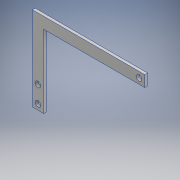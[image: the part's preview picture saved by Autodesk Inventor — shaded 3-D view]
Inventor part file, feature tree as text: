
AUTODESK INVENTOR PART (.ipt)
format: ipt  version: 2018.1 (Build 221171000, 171)  size: 113,664 bytes
history: native  units: mm
features: extrude x1, sketch x1
ambient origin geometry x8: Origin, YZ Plane, XZ Plane, XY Plane, X Axis, Y Axis, Z Axis, Center Point
bodies: Body1 (feature_tree)
feature tree (2):
  extrude  "押し出し4"  Depth=200.0mm
  sketch  "スケッチ1"
